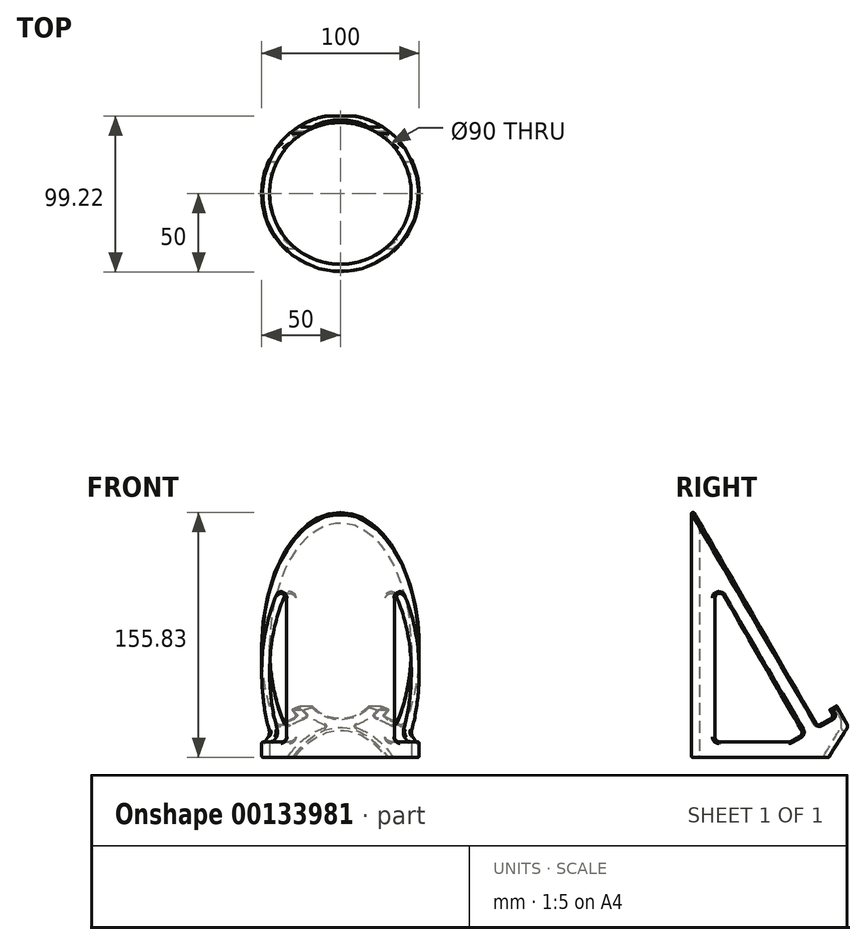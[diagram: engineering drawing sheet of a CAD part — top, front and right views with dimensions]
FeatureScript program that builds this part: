
annotation { "Feature Type Name" : "Feature", "Feature Type Description" : "" }
export const myFeature = defineFeature(function(context is Context, id is Id, definition is map)
    precondition{}
    {
        {
            var Q0;
            Q0=qCreatedBy(makeId("Top.planeOp"),FACE);
            var sketch = newSketch(context, id + "F0", { "sketchPlane" : qUnion([Q0])});
            skCircle(sketch, "E0", {"center": v(0, 0) * mm, "radius": 50 * mm});
            skCircle(sketch, "E1.0", {"center": v(0, 0) * mm, "radius": 45 * mm});
            skSolve(sketch);
        }
        {
            var Q0;
            Q0=makeQuery(id+"F0.imprint","IMPRINT",FACE,{"disambiguationData":[TD([[makeQuery(id+"F0.imprint","IMPRINT",EDGE,{"derivedFrom":sQuery(id+"F0.wireOp",EDGE,"E0")}),1.0]])]});
            extrude(context, id + "F1", {"entities" : qUnion([Q0]), "depth" : 200 * mm, "offsetDistance" : 25 * mm});
        }
        {
            var Q0;
            Q0=qCreatedBy(makeId("Right.planeOp"),FACE);
            var sketch = newSketch(context, id + "F2", { "sketchPlane" : qUnion([Q0])});
            skLineSegment(sketch, "E2", {"start": v(-70, 193.2) * mm, "end": v(29, 21.73) * mm});
            skLineSegment(sketch, "E3", {"start": v(31.73, 21) * mm, "end": v(38.66, 25) * mm});
            skLineSegment(sketch, "E4", {"start": v(39.4, 27.73) * mm, "end": v(37.9, 30.33) * mm});
            skLineSegment(sketch, "E5", {"start": v(80, -6.8) * mm, "end": v(80, 253.2) * mm});
            skLineSegment(sketch, "E6", {"start": v(80, 253.2) * mm, "end": v(-70, 253.2) * mm});
            skLineSegment(sketch, "E7", {"start": v(-70, 253.2) * mm, "end": v(-70, 193.2) * mm});
            skArc(sketch, "E8.filletArc", {"start": v(38.66, 25) * mm, "mid": v(39.6, 26.21) * mm, "end": v(39.4, 27.73) * mm});
            skPoint(sketch, "E9.visualSharp", {"position": v(30, 20) * mm});
            skArc(sketch, "E9.filletArc", {"start": v(29, 21.73) * mm, "mid": v(30.21, 20.8) * mm, "end": v(31.73, 21) * mm});
            skLineSegment(sketch, "E10", {"start": v(19.84, 17.6) * mm, "end": v(-29.4, 102.89) * mm});
            skLineSegment(sketch, "E11", {"start": v(-35, 101.39) * mm, "end": v(-35, 13) * mm});
            skLineSegment(sketch, "E12", {"start": v(-32, 10) * mm, "end": v(11.88, 10) * mm});
            skLineSegment(sketch, "E13", {"start": v(18.74, 13.5) * mm, "end": v(13.38, 10.4) * mm});
            skPoint(sketch, "E14.visualSharp", {"position": v(21.34, 15) * mm});
            skArc(sketch, "E14.filletArc", {"start": v(18.74, 13.5) * mm, "mid": v(20.14, 15.32) * mm, "end": v(19.84, 17.6) * mm});
            skPoint(sketch, "E15.visualSharp", {"position": v(12.68, 10) * mm});
            skArc(sketch, "E15.filletArc", {"start": v(11.88, 10) * mm, "mid": v(12.65, 10.1) * mm, "end": v(13.38, 10.4) * mm});
            skPoint(sketch, "E16.visualSharp", {"position": v(-35, 10) * mm});
            skArc(sketch, "E16.filletArc", {"start": v(-35, 13) * mm, "mid": v(-34.12, 10.88) * mm, "end": v(-32, 10) * mm});
            skPoint(sketch, "E17.visualSharp", {"position": v(-35, 112.58) * mm});
            skArc(sketch, "E17.filletArc", {"start": v(-29.4, 102.89) * mm, "mid": v(-32.78, 104.28) * mm, "end": v(-35, 101.39) * mm});
            skLineSegment(sketch, "E18", {"start": v(37.9, 30.33) * mm, "end": v(42.22, 32.83) * mm});
            skLineSegment(sketch, "E19", {"start": v(42.22, 32.83) * mm, "end": v(48.82, 21.4) * mm});
            skLineSegment(sketch, "E20", {"start": v(48.76, 18.3) * mm, "end": v(33.01, -6.8) * mm});
            skLineSegment(sketch, "E21", {"start": v(80, -6.8) * mm, "end": v(33.01, -6.8) * mm});
            skPoint(sketch, "E22.visualSharp", {"position": v(49.72, 19.84) * mm});
            skArc(sketch, "E22.filletArc", {"start": v(48.76, 18.3) * mm, "mid": v(49.22, 19.85) * mm, "end": v(48.82, 21.4) * mm});
            skSolve(sketch);
        }
        {
            var Q0;
            Q0 = qSketchRegion(id + "F2", true);
            extrude(context, id + "F3", {"entities" : qUnion([Q0]), "operationType" : NewBodyOperationType.REMOVE, "endBound" : BoundingType.SYMMETRIC, "oppositeDirection" : true, "depth" : 120 * mm, "offsetDistance" : 25 * mm});
        }
        {
            var Q0;
            Q0=qCreatedBy(makeId("Front.planeOp"),FACE);
            var sketch = newSketch(context, id + "F4", { "sketchPlane" : qUnion([Q0])});
            skCircle(sketch, "E23", {"center": v(0, 50) * mm, "radius": 25 * mm});
            skSolve(sketch);
        }
        {
            var Q0;
            Q0 = qSketchRegion(id + "F4", true);
            extrude(context, id + "F5", {"entities" : qUnion([Q0]), "operationType" : NewBodyOperationType.REMOVE, "oppositeDirection" : true, "depth" : 80 * mm, "offsetDistance" : 25 * mm});
        }
        {
            var Q0;
            Q0=makeQuery(id+"F3.boolean.opBoolean","INTERSECT",EDGE,{"derivedFrom":[makeQuery(id+"F1.opExtrude","SWEPT_FACE",FACE,{"disambiguationData":[OSD([sQuery(id+"F0.wireOp",EDGE,"E1.0")])]}),makeQuery(id+"F3.opExtrude","SWEPT_FACE",FACE,{"disambiguationData":[OSD([sQuery(id+"F2.wireOp",EDGE,"E20")])]})]});
            fillet(context, id + "F6", {"entities" : qUnion([Q0]), "radius" : 2 * mm, "tangentPropagation" : true, "allowEdgeOverflow" : false});
        }
        {
            var Q0;
            Q0=makeQuery(id+"F1.opExtrude","SWEPT_FACE",FACE,{"disambiguationData":[OSD([sQuery(id+"F0.wireOp",EDGE,"E0")])]});
            var Q1;
            Q1=makeQuery(id+"F1.opExtrude","SWEPT_FACE",FACE,{"disambiguationData":[OSD([sQuery(id+"F0.wireOp",EDGE,"E1.0")])]});
            fillet(context, id + "F7", {"entities" : qUnion([Q0, Q1]), "radius" : 1 * mm, "tangentPropagation" : true, "allowEdgeOverflow" : false});
        }
    });
